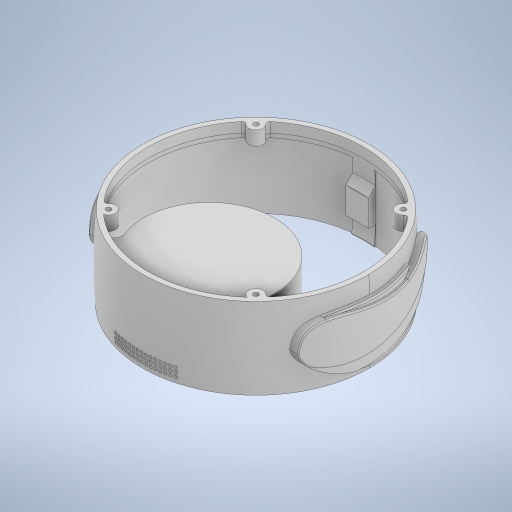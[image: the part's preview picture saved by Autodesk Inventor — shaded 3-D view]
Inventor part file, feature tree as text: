
AUTODESK INVENTOR PART (.ipt)
format: ipt  version: 2023 (Build 270158000, 158)  size: 2,163,200 bytes
history: native  units: mm
features: sketch x25, extrude x24, revolve x6, fillet x6, other x4, projected_geometry x4, mirror x3, chamfer x2, pattern_circular x1, hole x1
ambient origin geometry x8: Origin, YZ Plane, XZ Plane, XY Plane, X Axis, Y Axis, Z Axis, Center Point
bodies: Body1 (feature_tree)
feature tree (76):
  other  "솔리드1"
  revolve  "회전1"
  sketch  "스케치2"
  revolve  "회전2"
  revolve  "회전3"
  extrude  "돌출3"  Depth=120.0mm
  extrude  "돌출4"  Depth=140.0mm
  chamfer  "모따기1"  Distance=60.0mm
  fillet  "모깎기1"  Radius=130.0mm
  extrude  "돌출5"  Depth=160.0mm
  fillet  "모깎기2"  [1 undecoded]
  fillet  "모깎기3"  Radius=120.0mm
  extrude  "돌출6"  Depth=141.0mm
  other  "작업 평면2"
  extrude  "돌출7"  TaperAngle=90.0deg  [1 undecoded]
  mirror  "미러1"
  extrude  "돌출9"  Depth=4.0mm
  extrude  "돌출10"  TaperAngle=90.0deg  [1 undecoded]
  mirror  "미러2"
  sketch  "스케치13"
  extrude  "돌출11"  Depth=10.0mm
  extrude  "돌출12"  Depth=371.75mm TaperAngle=0.0deg
  sketch  "스케치15"
  extrude  "돌출13"  Depth=25.0mm
  extrude  "돌출14"  Depth=140.0mm
  pattern_circular  "원형 패턴1"  [2 undecoded]
  extrude  "돌출15"  Depth=103.5mm TaperAngle=0.0deg
  fillet  "모깎기4"  Radius=5.0mm
  other  "작업 평면4"
  extrude  "돌출16"  Depth=2.0mm
  chamfer  "모따기2"  Distance=90.0mm
  extrude  "돌출17"  Depth=103.5mm TaperAngle=0.0deg
  extrude  "돌출18"  Depth=1.0mm
  extrude  "돌출19"  Depth=0.5mm
  extrude  "돌출20"  Depth=7.0mm TaperAngle=0.0deg
  hole  "구멍1"  [1 undecoded]
  fillet  "모깎기5"  Radius=50.0mm
  extrude  "돌출21"  Depth=27.25mm TaperAngle=0.0deg
  extrude  "돌출22"  Depth=25.0mm
  extrude  "돌출23"  Depth=10.0mm TaperAngle=0.0deg
  other  "작업 평면5"
  sketch  "스케치27"
  sketch  "스케치28"
  sketch  "스케치29"
  extrude  "돌출25"  Depth=2.0mm
  revolve  "회전4"
  extrude  "돌출26"  Depth=18.0mm
  revolve  "회전5"
  extrude  "돌출27"  Depth=40.0mm TaperAngle=360.0deg
  revolve  "회전6"
  fillet  "모깎기11"  Radius=10.0mm
  mirror  "미러3"
  extrude  "돌출28"  Depth=77.0mm
  sketch  "스케치1"
  sketch  "스케치3"
  projected_geometry  "투영된 루프1"
  sketch  "스케치5"
  sketch  "스케치6"
  sketch  "스케치7"
  sketch  "스케치8"
  projected_geometry  "투영된 루프2"
  sketch  "스케치9"
  sketch  "스케치11"
  sketch  "스케치12"
  sketch  "스케치16"
  sketch  "스케치17"
  sketch  "스케치18"
  sketch  "스케치20"
  sketch  "스케치21"
  sketch  "스케치22"
  sketch  "스케치23"
  projected_geometry  "투영된 루프3"
  sketch  "스케치24"
  sketch  "스케치25"
  projected_geometry  "투영된 루프4"
  sketch  "스케치26"
note: 6 required parameter values undecoded (feature->parameter linkage not recoverable at this tier; creation-order binding heuristic only, values carry confidence <= 0.55)
